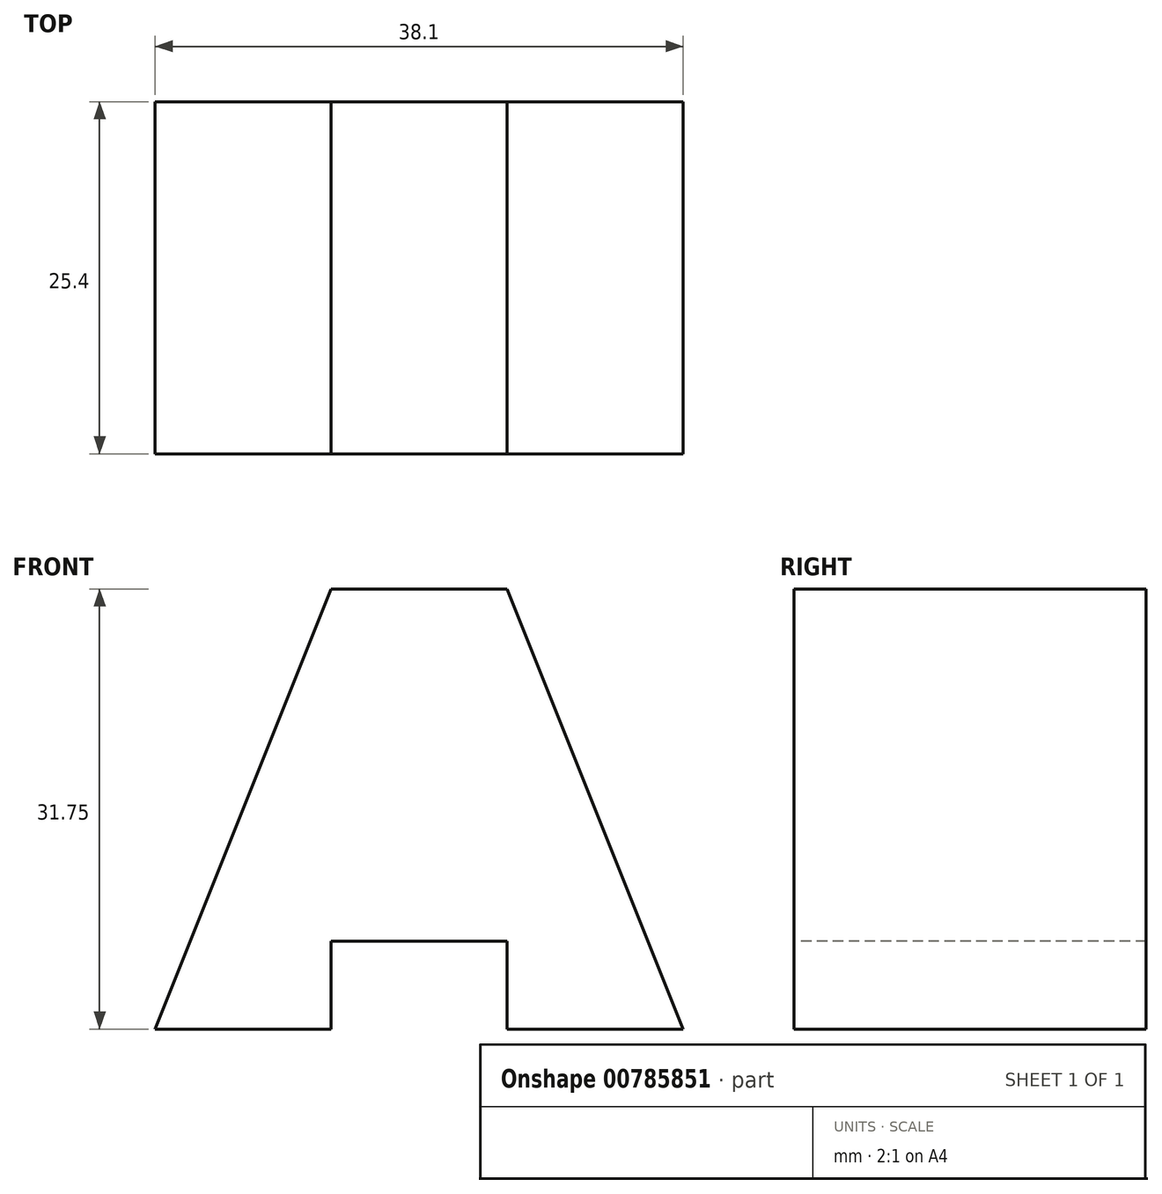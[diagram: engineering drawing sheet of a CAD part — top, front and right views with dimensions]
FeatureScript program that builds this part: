
annotation { "Feature Type Name" : "Feature", "Feature Type Description" : "" }
export const myFeature = defineFeature(function(context is Context, id is Id, definition is map)
    precondition{}
    {
        {
            var Q0;
            Q0=qCreatedBy(makeId("Front.planeOp"),FACE);
            var sketch = newSketch(context, id + "F0", { "sketchPlane" : qUnion([Q0])});
            skLineSegment(sketch, "E0", {"start": v(0, 0) * mm, "end": v(38.1, 0) * mm});
            skLineSegment(sketch, "E1", {"start": v(38.1, 0) * mm, "end": v(38.1, 31.75) * mm});
            skLineSegment(sketch, "E2", {"start": v(38.1, 31.75) * mm, "end": v(0, 31.75) * mm});
            skLineSegment(sketch, "E3", {"start": v(0, 31.75) * mm, "end": v(0, 0) * mm});
            skSolve(sketch);
        }
        {
            var Q0;
            Q0=makeQuery(id+"F0.imprint","IMPRINT",FACE,{"disambiguationData":[TD([[makeQuery(id+"F0.imprint","IMPRINT",EDGE,{"derivedFrom":sQuery(id+"F0.wireOp",EDGE,"E0")}),1.0]])]});
            extrude(context, id + "F1", {"entities" : qUnion([Q0]), "depth" : 25.4 * mm, "offsetDistance" : 25.4 * mm});
        }
        {
            var Q0;
            Q0=makeQuery(id+"F1.opExtrude","CAP_FACE",FACE,{"disambiguationData":[OSD([sQuery(id+"F0.wireOp",EDGE,"E0"),sQuery(id+"F0.wireOp",EDGE,"E1"),sQuery(id+"F0.wireOp",EDGE,"E2"),sQuery(id+"F0.wireOp",EDGE,"E3")])],"isStart":false});
            var sketch = newSketch(context, id + "F2", { "sketchPlane" : qUnion([Q0])});
            skLineSegment(sketch, "E4", {"start": v(0, 31.75) * mm, "end": v(12.7, 31.75) * mm});
            skLineSegment(sketch, "E5", {"start": v(38.1, 31.75) * mm, "end": v(25.4, 31.75) * mm});
            skLineSegment(sketch, "E6", {"start": v(25.4, 31.75) * mm, "end": v(38.1, 0) * mm});
            skLineSegment(sketch, "E7", {"start": v(12.7, 31.75) * mm, "end": v(0, 0) * mm});
            skSolve(sketch);
        }
        {
            var Q0;
            Q0=makeQuery(id+"F2.imprint","IMPRINT",FACE,{"disambiguationData":[TD([[makeQuery(id+"F2.imprint","IMPRINT",EDGE,{"derivedFrom":sQuery(id+"F2.wireOp",EDGE,"E4")}),1.0]])]});
            extrude(context, id + "F3", {"entities" : qUnion([Q0]), "operationType" : NewBodyOperationType.REMOVE, "oppositeDirection" : true, "depth" : 25.4 * mm, "offsetDistance" : 25.4 * mm});
        }
        {
            var Q0;
            Q0=makeQuery(id+"F1.opExtrude","CAP_FACE",FACE,{"disambiguationData":[OSD([sQuery(id+"F0.wireOp",EDGE,"E0"),sQuery(id+"F0.wireOp",EDGE,"E1"),sQuery(id+"F0.wireOp",EDGE,"E2"),sQuery(id+"F0.wireOp",EDGE,"E3")])],"isStart":false});
            var sketch = newSketch(context, id + "F4", { "sketchPlane" : qUnion([Q0])});
            skLineSegment(sketch, "E8", {"start": v(38.1, 31.75) * mm, "end": v(25.4, 31.75) * mm});
            skLineSegment(sketch, "E9", {"start": v(25.4, 31.75) * mm, "end": v(38.1, 0) * mm});
            skSolve(sketch);
        }
        {
            var Q0;
            Q0=makeQuery(id+"F4.imprint","IMPRINT",FACE,{"disambiguationData":[TD([[makeQuery(id+"F4.imprint","IMPRINT",EDGE,{"derivedFrom":sQuery(id+"F4.wireOp",EDGE,"E8")}),1.0]])]});
            extrude(context, id + "F5", {"entities" : qUnion([Q0]), "operationType" : NewBodyOperationType.REMOVE, "oppositeDirection" : true, "depth" : 25.4 * mm, "offsetDistance" : 25.4 * mm});
        }
        {
            var Q0;
            Q0=makeQuery(id+"F1.opExtrude","CAP_FACE",FACE,{"disambiguationData":[OSD([sQuery(id+"F0.wireOp",EDGE,"E0"),sQuery(id+"F0.wireOp",EDGE,"E1"),sQuery(id+"F0.wireOp",EDGE,"E2"),sQuery(id+"F0.wireOp",EDGE,"E3")])],"isStart":false});
            var sketch = newSketch(context, id + "F6", { "sketchPlane" : qUnion([Q0])});
            skLineSegment(sketch, "E10", {"start": v(0, 0) * mm, "end": v(12.7, 0) * mm});
            skLineSegment(sketch, "E11", {"start": v(12.7, 0) * mm, "end": v(12.7, 6.35) * mm});
            skLineSegment(sketch, "E12", {"start": v(12.7, 6.35) * mm, "end": v(25.4, 6.35) * mm});
            skLineSegment(sketch, "E13", {"start": v(25.4, 6.35) * mm, "end": v(25.4, 0) * mm});
            skLineSegment(sketch, "E14", {"start": v(25.4, 0) * mm, "end": v(38.1, 0) * mm});
            skSolve(sketch);
        }
        {
            var Q0;
            {var subQ0=sQuery(id+"F6.wireOp",EDGE,"E11");Q0=makeQuery(id+"F6.imprint","IMPRINT",FACE,{"disambiguationData":[TD([[makeQuery(id+"F6.imprint","IMPRINT",EDGE,{"derivedFrom":subQ0}),-1.0]])]});}
            extrude(context, id + "F7", {"entities" : qUnion([Q0]), "operationType" : NewBodyOperationType.REMOVE, "oppositeDirection" : true, "depth" : 25.4 * mm, "offsetDistance" : 25.4 * mm});
        }
    });
